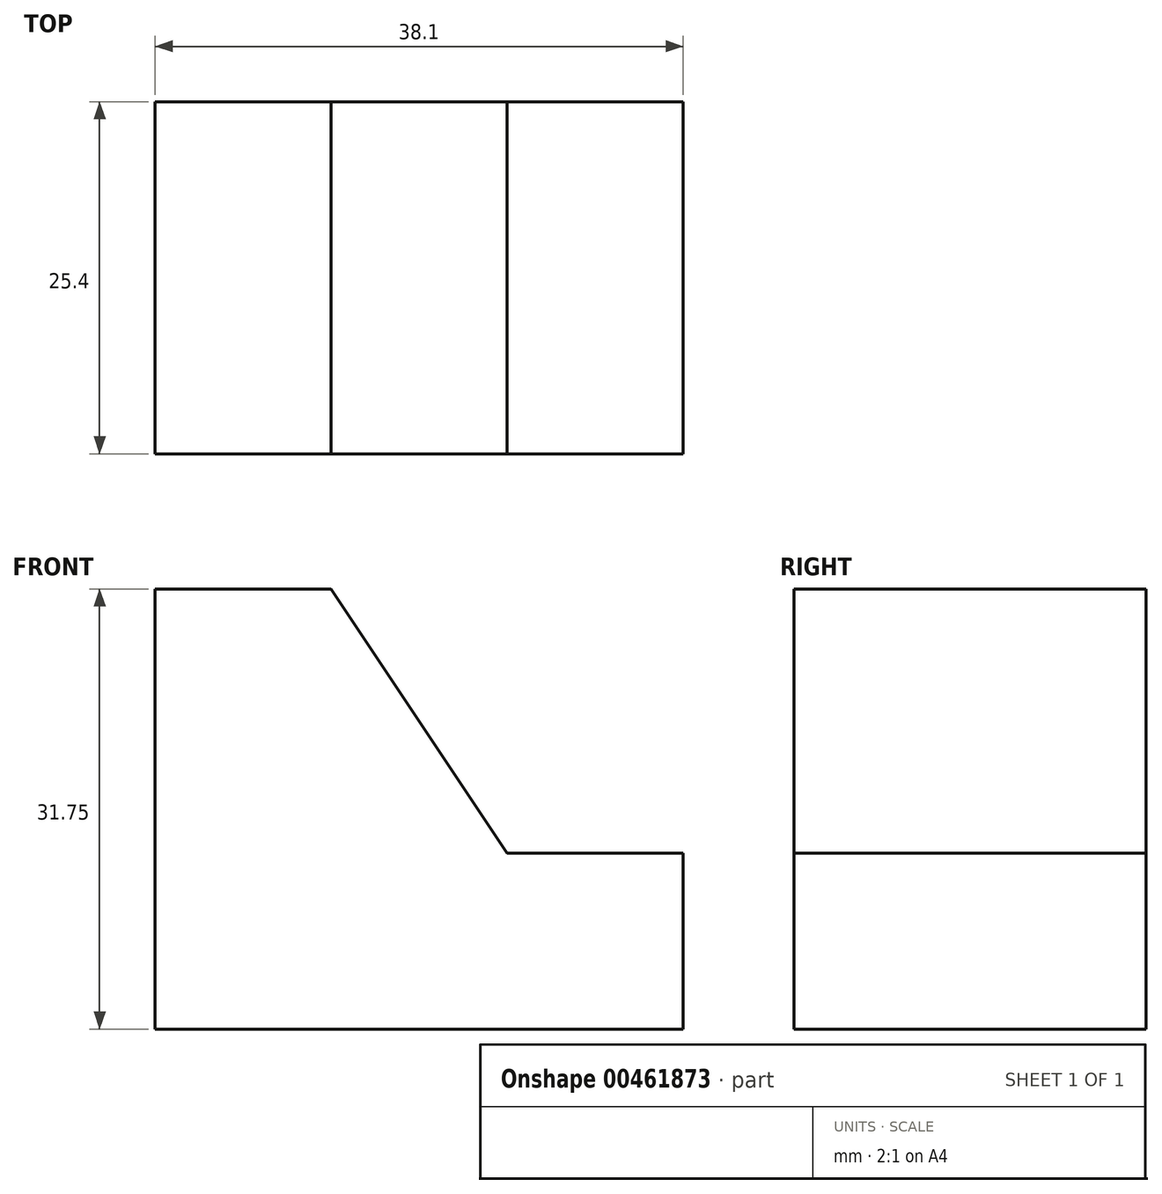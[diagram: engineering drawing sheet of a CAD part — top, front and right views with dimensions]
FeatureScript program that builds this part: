
annotation { "Feature Type Name" : "Feature", "Feature Type Description" : "" }
export const myFeature = defineFeature(function(context is Context, id is Id, definition is map)
    precondition{}
    {
        {
            var Q0;
            Q0=qCreatedBy(makeId("Front.planeOp"),FACE);
            var sketch = newSketch(context, id + "F0", { "sketchPlane" : qUnion([Q0])});
            skLineSegment(sketch, "E0.bottom", {"start": v(0, 0) * mm, "end": v(38.1, 0) * mm});
            skLineSegment(sketch, "E0.top", {"start": v(0, 31.75) * mm, "end": v(38.1, 31.75) * mm});
            skLineSegment(sketch, "E0.left", {"start": v(0, 0) * mm, "end": v(0, 31.75) * mm});
            skLineSegment(sketch, "E0.right", {"start": v(38.1, 0) * mm, "end": v(38.1, 31.75) * mm});
            skSolve(sketch);
        }
        {
            var Q0;
            Q0 = qSketchRegion(id + "F0", true);
            extrude(context, id + "F1", {"entities" : qUnion([Q0]), "depth" : 25.4 * mm});
        }
        {
            var Q0;
            Q0=makeQuery(id+"F1.opExtrude","CAP_FACE",FACE,{"disambiguationData":[OSD([sQuery(id+"F0.wireOp",EDGE,"E0.bottom"),sQuery(id+"F0.wireOp",EDGE,"E0.top"),sQuery(id+"F0.wireOp",EDGE,"E0.left"),sQuery(id+"F0.wireOp",EDGE,"E0.right")])],"isStart":false});
            var sketch = newSketch(context, id + "F2", { "sketchPlane" : qUnion([Q0])});
            skLineSegment(sketch, "E1", {"start": v(0, 31.75) * mm, "end": v(12.7, 31.75) * mm});
            skLineSegment(sketch, "E2", {"start": v(12.7, 31.75) * mm, "end": v(25.4, 12.7) * mm});
            skLineSegment(sketch, "E3", {"start": v(25.4, 12.7) * mm, "end": v(38.1, 12.7) * mm});
            skLineSegment(sketch, "E4", {"start": v(38.1, 12.7) * mm, "end": v(38.1, 0) * mm});
            skSolve(sketch);
        }
        {
            var Q0;
            {var subQ0=sQuery(id+"F2.wireOp",EDGE,"E2");Q0=makeQuery(id+"F2.imprint","IMPRINT",FACE,{"disambiguationData":[TD([[makeQuery(id+"F2.imprint","IMPRINT",EDGE,{"derivedFrom":subQ0}),1.0]])]});}
            extrude(context, id + "F3", {"entities" : qUnion([Q0]), "operationType" : NewBodyOperationType.REMOVE, "oppositeDirection" : true, "depth" : 25.4 * mm});
        }
    });
